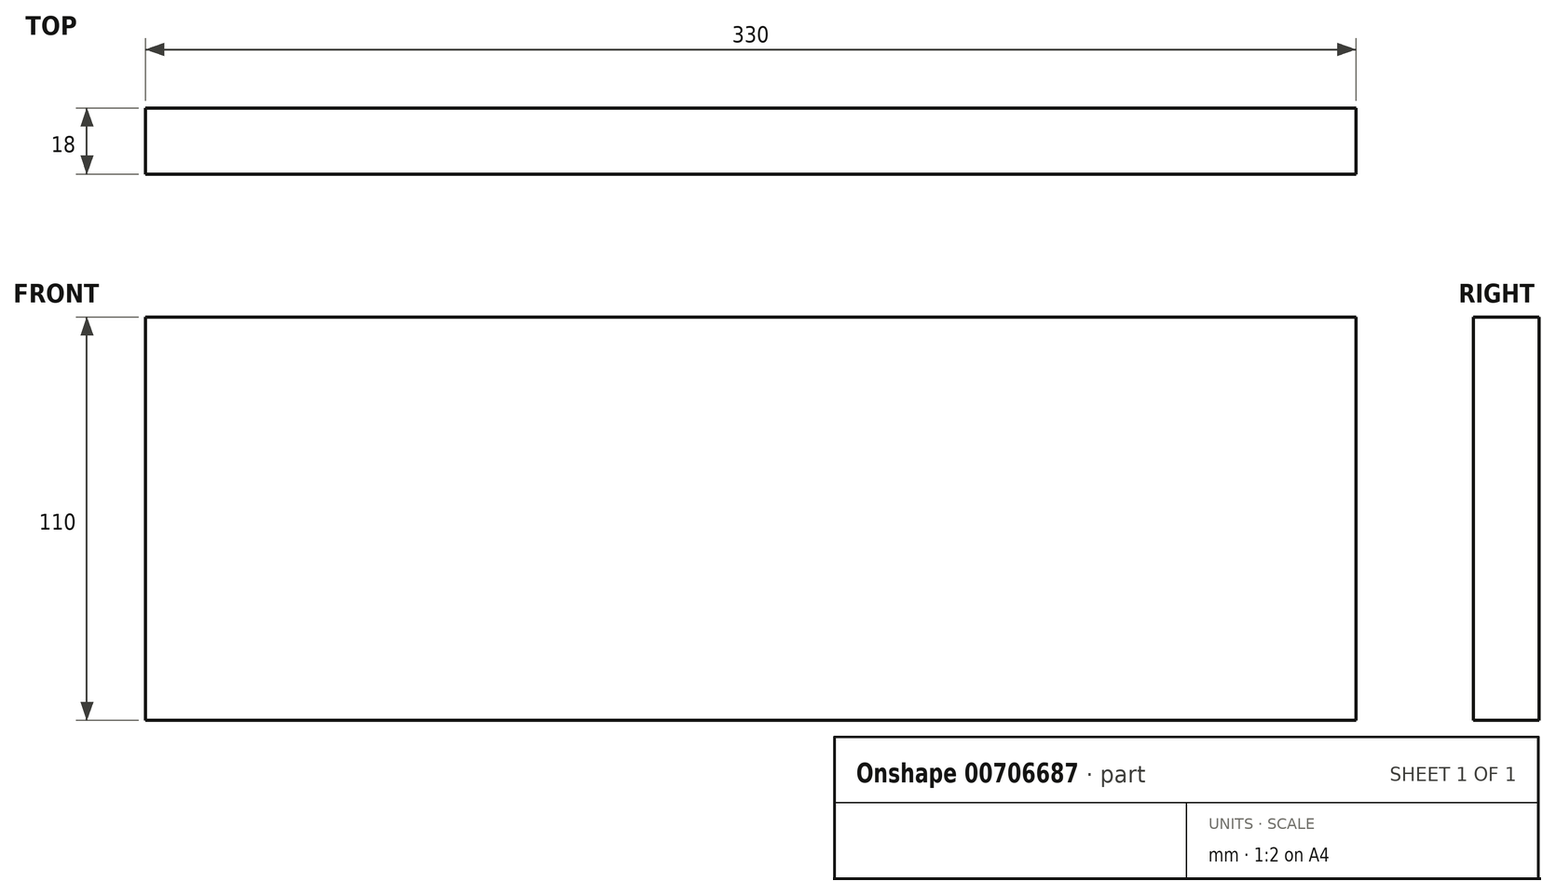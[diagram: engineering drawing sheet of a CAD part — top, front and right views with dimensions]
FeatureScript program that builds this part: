
annotation { "Feature Type Name" : "Feature", "Feature Type Description" : "" }
export const myFeature = defineFeature(function(context is Context, id is Id, definition is map)
    precondition{}
    {
        {
            var Q0;
            Q0=qCreatedBy(makeId("Front.planeOp"),FACE);
            var sketch = newSketch(context, id + "F0", { "sketchPlane" : qUnion([Q0])});
            skLineSegment(sketch, "E0.bottom", {"start": v(-165, -55) * mm, "end": v(165, -55) * mm});
            skLineSegment(sketch, "E0.top", {"start": v(-165, 55) * mm, "end": v(165, 55) * mm});
            skLineSegment(sketch, "E0.left", {"start": v(-165, -55) * mm, "end": v(-165, 55) * mm});
            skLineSegment(sketch, "E0.right", {"start": v(165, -55) * mm, "end": v(165, 55) * mm});
            skPoint(sketch, "E0.middle", {"position": v(0, 0) * mm});
            skSolve(sketch);
        }
        {
            var Q0;
            Q0=makeQuery(id+"F0.imprint","IMPRINT",FACE,{"disambiguationData":[TD([[makeQuery(id+"F0.imprint","IMPRINT",EDGE,{"derivedFrom":sQuery(id+"F0.wireOp",EDGE,"E0.bottom")}),1.0]])]});
            extrude(context, id + "F1", {"entities" : qUnion([Q0]), "depth" : 18 * mm, "offsetDistance" : 25 * mm, "symmetric" : true});
        }
    });
